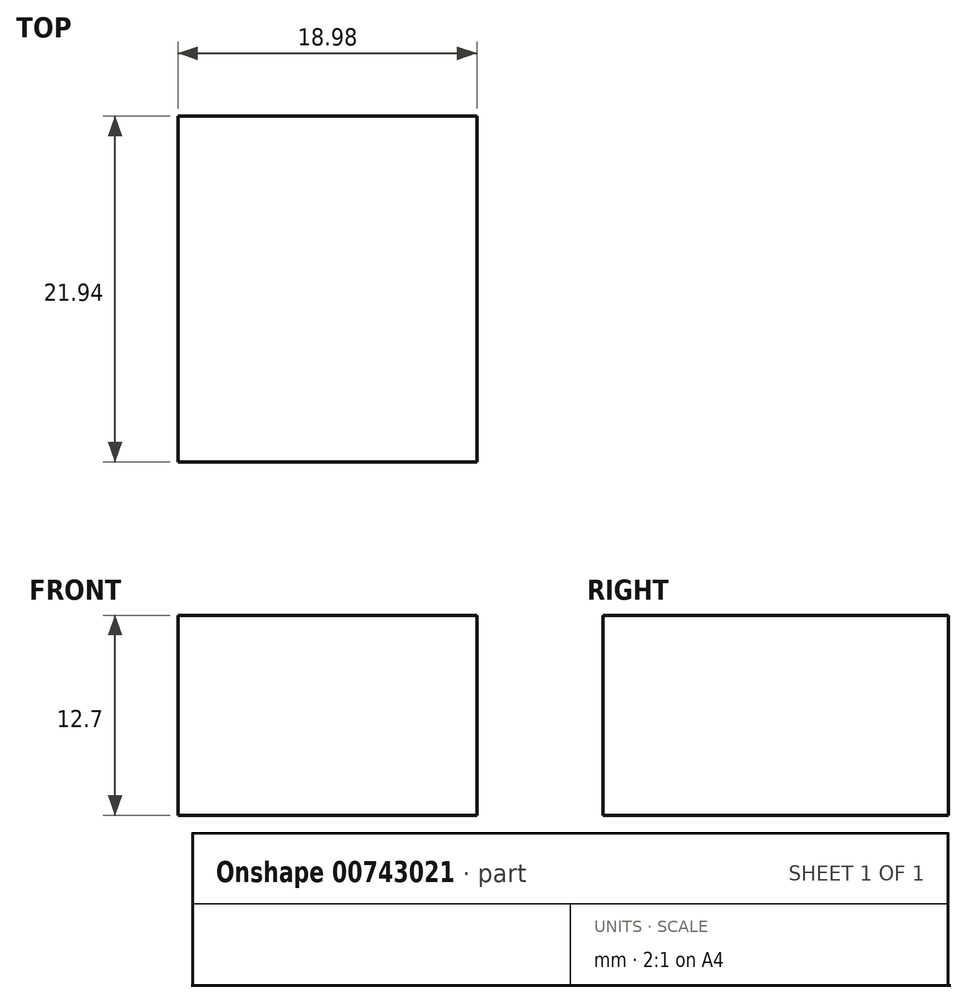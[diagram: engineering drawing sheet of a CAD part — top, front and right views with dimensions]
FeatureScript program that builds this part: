
annotation { "Feature Type Name" : "Feature", "Feature Type Description" : "" }
export const myFeature = defineFeature(function(context is Context, id is Id, definition is map)
    precondition{}
    {
        {
            var Q0;
            Q0=qCreatedBy(makeId("Top.planeOp"),FACE);
            var sketch = newSketch(context, id + "F0", { "sketchPlane" : qUnion([Q0])});
            skLineSegment(sketch, "E0.bottom", {"start": v(-9.49, 13.4) * mm, "end": v(9.49, 13.4) * mm});
            skLineSegment(sketch, "E0.top", {"start": v(-9.49, -8.54) * mm, "end": v(9.49, -8.54) * mm});
            skLineSegment(sketch, "E0.left", {"start": v(-9.49, 13.4) * mm, "end": v(-9.49, -8.54) * mm});
            skLineSegment(sketch, "E0.right", {"start": v(9.49, 13.4) * mm, "end": v(9.49, -8.54) * mm});
            skPoint(sketch, "E0.middle", {"position": v(0, 2.43) * mm});
            skSolve(sketch);
        }
        {
            var Q0;
            Q0=makeQuery(id+"F0.imprint","IMPRINT",FACE,{"disambiguationData":[TD([[makeQuery(id+"F0.imprint","IMPRINT",EDGE,{"derivedFrom":sQuery(id+"F0.wireOp",EDGE,"E0.bottom")}),-1.0]])]});
            extrude(context, id + "F1", {"entities" : qUnion([Q0]), "depth" : 12.7 * mm, "offsetDistance" : 25.4 * mm});
        }
    });
